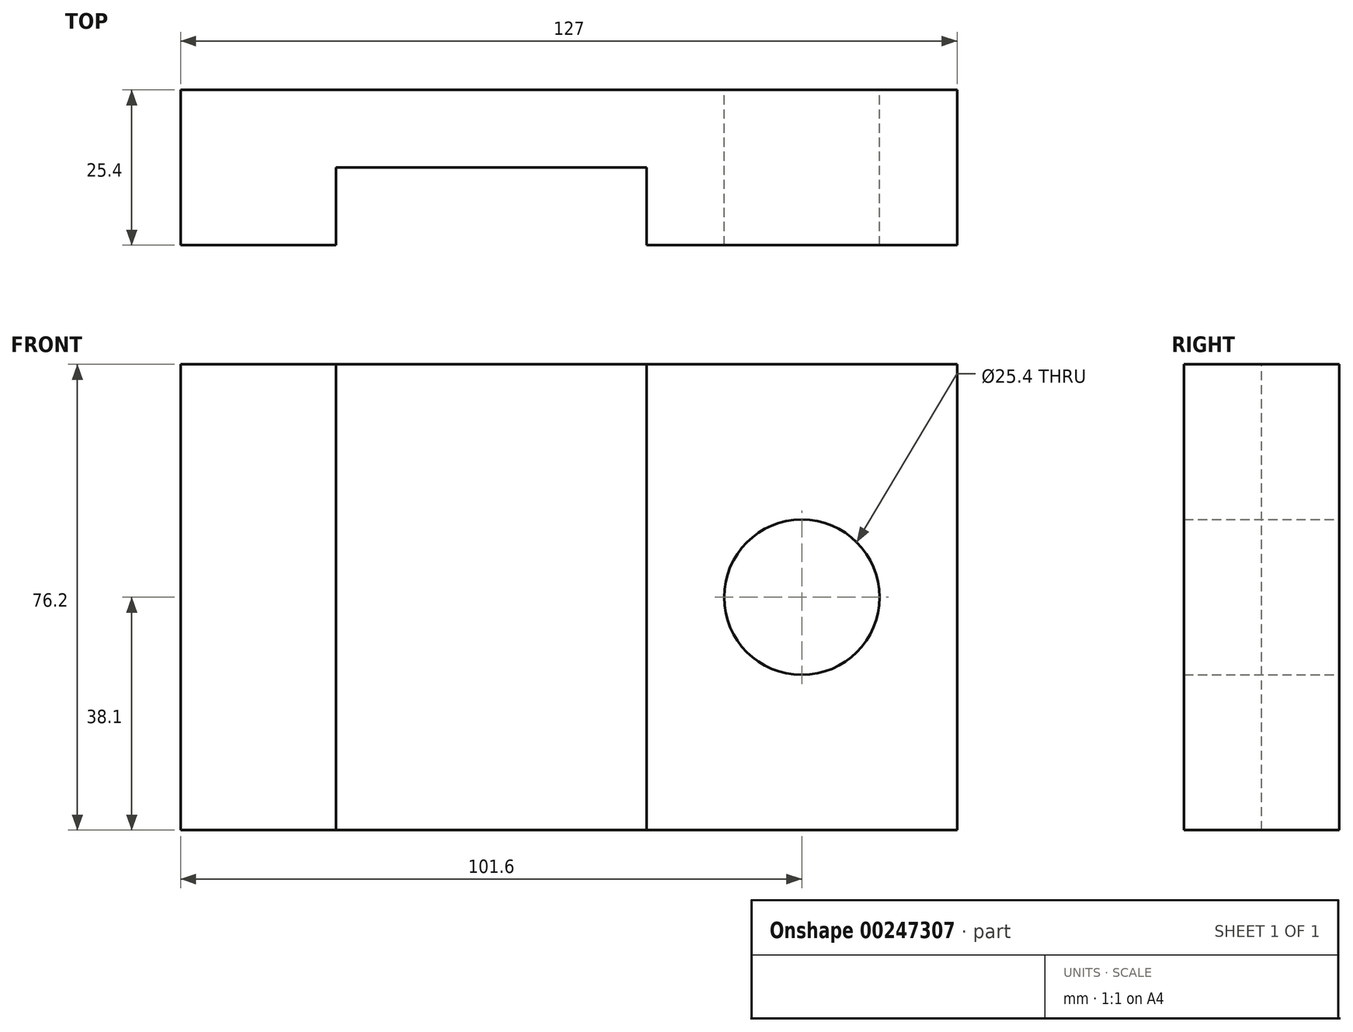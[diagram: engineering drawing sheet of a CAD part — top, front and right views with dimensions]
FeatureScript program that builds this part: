
annotation { "Feature Type Name" : "Feature", "Feature Type Description" : "" }
export const myFeature = defineFeature(function(context is Context, id is Id, definition is map)
    precondition{}
    {
        {
            var Q0;
            Q0=qCreatedBy(makeId("Front.planeOp"),FACE);
            var sketch = newSketch(context, id + "F0", { "sketchPlane" : qUnion([Q0])});
            skLineSegment(sketch, "E0", {"start": v(0, 0) * mm, "end": v(0, 76.2) * mm});
            skLineSegment(sketch, "E1", {"start": v(0, 76.2) * mm, "end": v(50.8, 76.2) * mm});
            skLineSegment(sketch, "E2", {"start": v(50.8, 76.2) * mm, "end": v(50.8, 0) * mm});
            skLineSegment(sketch, "E3", {"start": v(0, 0) * mm, "end": v(50.8, 0) * mm});
            skLineSegment(sketch, "E4", {"start": v(50.8, 76.2) * mm, "end": v(101.6, 76.2) * mm});
            skLineSegment(sketch, "E5", {"start": v(101.6, 76.2) * mm, "end": v(101.6, 0) * mm});
            skLineSegment(sketch, "E6", {"start": v(101.6, 0) * mm, "end": v(50.8, 0) * mm});
            skLineSegment(sketch, "E7", {"start": v(0, 76.2) * mm, "end": v(-25.4, 76.2) * mm});
            skLineSegment(sketch, "E8", {"start": v(-25.4, 76.2) * mm, "end": v(-25.4, 0) * mm});
            skLineSegment(sketch, "E9", {"start": v(0, 0) * mm, "end": v(-25.4, 0) * mm});
            skCircle(sketch, "E10", {"center": v(76.2, 38.1) * mm, "radius": 12.7 * mm});
            skPoint(sketch, "E10.centerSnap0", {"position": v(101.6, 38.1) * mm});
            skPoint(sketch, "E10.centerSnap1", {"position": v(76.2, 0) * mm});
            skSolve(sketch);
        }
        {
            var Q0;
            Q0=makeQuery(id+"F0.imprint","IMPRINT",FACE,{"disambiguationData":[TD([[makeQuery(id+"F0.imprint","IMPRINT",EDGE,{"derivedFrom":sQuery(id+"F0.wireOp",EDGE,"E0")}),1.0]])]});
            extrude(context, id + "F1", {"entities" : qUnion([Q0]), "depth" : 25.4 * mm});
        }
        {
            var Q0;
            Q0=makeQuery(id+"F0.imprint","IMPRINT",FACE,{"disambiguationData":[TD([[makeQuery(id+"F0.imprint","IMPRINT",EDGE,{"derivedFrom":sQuery(id+"F0.wireOp",EDGE,"E0")}),-1.0]])]});
            extrude(context, id + "F2", {"entities" : qUnion([Q0]), "operationType" : NewBodyOperationType.ADD, "depth" : 12.7 * mm});
        }
        {
            var Q0;
            Q0=makeQuery(id+"F0.imprint","IMPRINT",FACE,{"disambiguationData":[TD([[makeQuery(id+"F0.imprint","IMPRINT",EDGE,{"derivedFrom":sQuery(id+"F0.wireOp",EDGE,"E2")}),1.0]])]});
            extrude(context, id + "F3", {"entities" : qUnion([Q0]), "operationType" : NewBodyOperationType.ADD, "depth" : 25.4 * mm});
        }
    });
